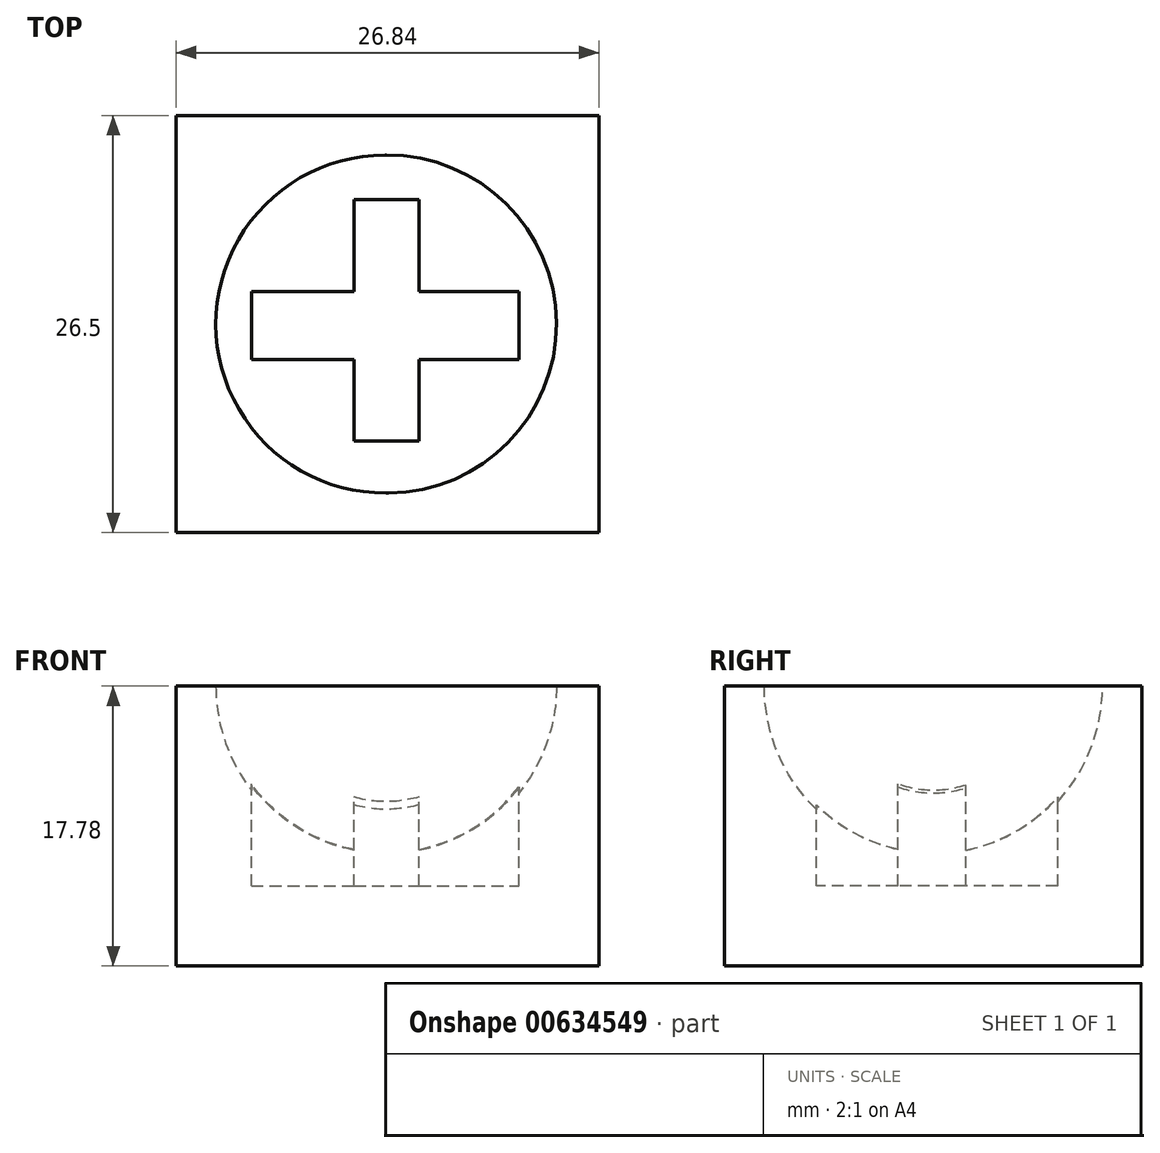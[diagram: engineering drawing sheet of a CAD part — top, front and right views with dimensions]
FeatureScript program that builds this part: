
annotation { "Feature Type Name" : "Feature", "Feature Type Description" : "" }
export const myFeature = defineFeature(function(context is Context, id is Id, definition is map)
    precondition{}
    {
        {
            var Q0;
            Q0=qCreatedBy(makeId("Top.planeOp"),FACE);
            var sketch = newSketch(context, id + "F0", { "sketchPlane" : qUnion([Q0])});
            skLineSegment(sketch, "E0.bottom", {"start": v(13.42, 13.25) * mm, "end": v(-13.42, 13.25) * mm});
            skLineSegment(sketch, "E0.top", {"start": v(13.42, -13.25) * mm, "end": v(-13.42, -13.25) * mm});
            skLineSegment(sketch, "E0.left", {"start": v(13.42, 13.25) * mm, "end": v(13.42, -13.25) * mm});
            skLineSegment(sketch, "E0.right", {"start": v(-13.42, 13.25) * mm, "end": v(-13.42, -13.25) * mm});
            skPoint(sketch, "E0.middle", {"position": v(0, 0) * mm});
            skSolve(sketch);
        }
        {
            var Q0;
            Q0 = qSketchRegion(id + "F0", true);
            extrude(context, id + "F1", {"entities" : qUnion([Q0]), "depth" : 17.78 * mm, "offsetDistance" : 25.4 * mm});
        }
        {
            var Q0;
            Q0=makeQuery(id+"F1.opExtrude","CAP_FACE",FACE,{"disambiguationData":[OSD([sQuery(id+"F0.wireOp",EDGE,"E0.bottom"),sQuery(id+"F0.wireOp",EDGE,"E0.top"),sQuery(id+"F0.wireOp",EDGE,"E0.left"),sQuery(id+"F0.wireOp",EDGE,"E0.right")])],"isStart":false});
            var sketch = newSketch(context, id + "F2", { "sketchPlane" : qUnion([Q0])});
            skArc(sketch, "E1", {"start": v(-0.01, -10.73) * mm, "mid": v(10.73, 0.07) * mm, "end": v(-0.16, 10.73) * mm});
            skLineSegment(sketch, "E2", {"start": v(-0.16, 10.73) * mm, "end": v(-0.01, -10.73) * mm});
            skSolve(sketch);
        }
        {
            var Q0;
            Q0=makeQuery(id+"F2.imprint","IMPRINT",FACE,{"disambiguationData":[TD([[makeQuery(id+"F2.imprint","IMPRINT",EDGE,{"derivedFrom":sQuery(id+"F2.wireOp",EDGE,"E1")}),1.0]])]});
            var Q1;
            Q1=sQuery(id+"F2.wireOp",EDGE,"E1");
            var Q2;
            Q2=sQuery(id+"F2.wireOp",EDGE,"E2");
            revolve(context, id + "F3", {"operationType" : NewBodyOperationType.REMOVE, "entities" : qUnion([Q0]), "surfaceEntities" : qUnion([Q1]), "axis" : qUnion([Q2]), "revolveType" : RevolveType.ONE_DIRECTION, "oppositeDirection" : true, "angle" : 180 * degree});
        }
        {
            var Q0;
            Q0=makeQuery(id+"F2.imprint","IMPRINT",FACE,{"disambiguationData":[TD([[makeQuery(id+"F2.imprint","IMPRINT",EDGE,{"derivedFrom":sQuery(id+"F2.wireOp",EDGE,"E1")}),1.0]])]});
            var sketch = newSketch(context, id + "F4", { "sketchPlane" : qUnion([Q0])});
            skLineSegment(sketch, "E3.bottom", {"start": v(-2.12, 7.91) * mm, "end": v(2, 7.91) * mm});
            skLineSegment(sketch, "E3.top", {"start": v(-2.12, -7.44) * mm, "end": v(2, -7.44) * mm});
            skLineSegment(sketch, "E3.left", {"start": v(-2.12, 7.91) * mm, "end": v(-2.12, 2.06) * mm});
            skLineSegment(sketch, "E3.right", {"start": v(2, 7.91) * mm, "end": v(2, 2.06) * mm});
            skLineSegment(sketch, "E4.bottom", {"start": v(-8.64, 2.06) * mm, "end": v(-2.12, 2.06) * mm});
            skLineSegment(sketch, "E4.top", {"start": v(-8.64, -2.26) * mm, "end": v(-2.12, -2.26) * mm});
            skLineSegment(sketch, "E4.left", {"start": v(-8.64, 2.06) * mm, "end": v(-8.64, -2.26) * mm});
            skLineSegment(sketch, "E4.right", {"start": v(8.34, 2.06) * mm, "end": v(8.34, -2.26) * mm});
            skLineSegment(sketch, "E5.trimOffspring", {"start": v(-2.12, -2.26) * mm, "end": v(-2.12, -7.44) * mm});
            skLineSegment(sketch, "E6.trimOffspring", {"start": v(2, -2.26) * mm, "end": v(2, -7.44) * mm});
            skLineSegment(sketch, "E7.trimOffspring", {"start": v(2, 2.06) * mm, "end": v(8.34, 2.06) * mm});
            skLineSegment(sketch, "E8.trimOffspring", {"start": v(2, -2.26) * mm, "end": v(8.34, -2.26) * mm});
            skSolve(sketch);
        }
        {
            var Q0;
            {var subQ0=sQuery(id+"F4.wireOp",EDGE,"E3.right");Q0=makeQuery(id+"F4.imprint","IMPRINT",FACE,{"disambiguationData":[TD([[makeQuery(id+"F4.imprint","IMPRINT",EDGE,{"derivedFrom":subQ0}),-1.0]])]});}
            var Q1;
            {var subQ5=sQuery(id+"F4.wireOp",EDGE,"E3.left");Q1=makeQuery(id+"F4.imprint","IMPRINT",FACE,{"disambiguationData":[TD([[makeQuery(id+"F4.imprint","IMPRINT",EDGE,{"derivedFrom":subQ5}),1.0]])]});}
            var Q2;
            Q2=sQuery(id+"F4.wireOp",EDGE,"E4.bottom");
            var Q3;
            Q3=sQuery(id+"F4.wireOp",EDGE,"E4.left");
            var Q4;
            Q4=sQuery(id+"F4.wireOp",EDGE,"E4.top");
            var Q5;
            Q5=sQuery(id+"F4.wireOp",EDGE,"E5.trimOffspring");
            var Q6;
            Q6=sQuery(id+"F4.wireOp",EDGE,"E3.top");
            var Q7;
            Q7=sQuery(id+"F4.wireOp",EDGE,"E6.trimOffspring");
            var Q8;
            Q8=sQuery(id+"F4.wireOp",EDGE,"E8.trimOffspring");
            var Q9;
            Q9=sQuery(id+"F4.wireOp",EDGE,"E4.right");
            var Q10;
            Q10=sQuery(id+"F4.wireOp",EDGE,"E7.trimOffspring");
            var Q11;
            Q11=sQuery(id+"F4.wireOp",EDGE,"E3.right");
            var Q12;
            Q12=sQuery(id+"F4.wireOp",EDGE,"E3.bottom");
            var Q13;
            Q13=sQuery(id+"F4.wireOp",EDGE,"E3.left");
            extrude(context, id + "F5", {"entities" : qUnion([Q0, Q1]), "operationType" : NewBodyOperationType.REMOVE, "surfaceEntities" : qUnion([Q2, Q3, Q4, Q5, Q6, Q7, Q8, Q9, Q10, Q11, Q12, Q13]), "oppositeDirection" : true, "depth" : 12.7 * mm, "offsetDistance" : 25.4 * mm});
        }
    });
